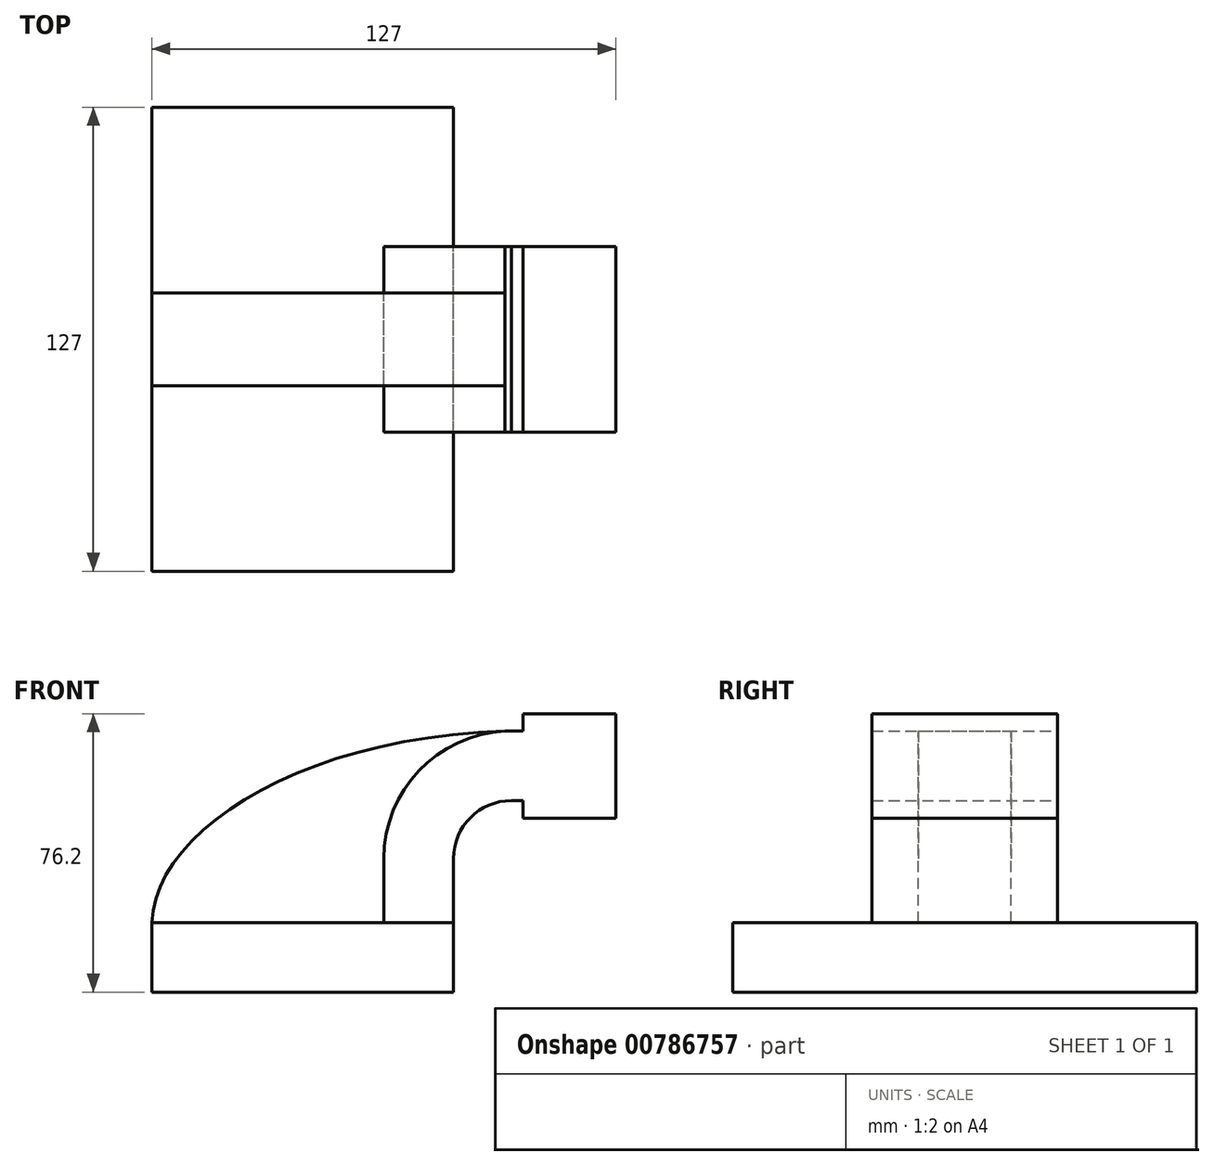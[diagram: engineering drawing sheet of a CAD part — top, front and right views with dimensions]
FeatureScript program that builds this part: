
annotation { "Feature Type Name" : "Feature", "Feature Type Description" : "" }
export const myFeature = defineFeature(function(context is Context, id is Id, definition is map)
    precondition{}
    {
        {
            var Q0;
            Q0=qCreatedBy(makeId("Front.planeOp"),FACE);
            var sketch = newSketch(context, id + "F0", { "sketchPlane" : qUnion([Q0])});
            skLineSegment(sketch, "E0.bottom", {"start": v(-41.28, 9.52) * mm, "end": v(41.27, 9.53) * mm});
            skLineSegment(sketch, "E0.top", {"start": v(-41.28, -9.53) * mm, "end": v(41.28, -9.53) * mm});
            skLineSegment(sketch, "E0.left", {"start": v(-41.28, 9.52) * mm, "end": v(-41.27, -9.53) * mm});
            skLineSegment(sketch, "E0.right", {"start": v(41.28, 9.53) * mm, "end": v(41.28, -9.52) * mm});
            skPoint(sketch, "E0.middle", {"position": v(0, 0) * mm});
            skLineSegment(sketch, "E1.bottom", {"start": v(60.32, 66.68) * mm, "end": v(111.12, 66.68) * mm});
            skLineSegment(sketch, "E1.top", {"start": v(60.32, 38.1) * mm, "end": v(111.12, 38.1) * mm});
            skLineSegment(sketch, "E1.left", {"start": v(60.32, 66.68) * mm, "end": v(60.32, 38.1) * mm});
            skLineSegment(sketch, "E1.right", {"start": v(111.12, 66.68) * mm, "end": v(111.12, 38.1) * mm});
            skPoint(sketch, "E1.middle", {"position": v(85.72, 52.39) * mm});
            skLineSegment(sketch, "E2", {"start": v(41.27, 9.53) * mm, "end": v(41.27, 27) * mm});
            skArc(sketch, "E3", {"start": v(41.27, 27) * mm, "mid": v(45.92, 38.23) * mm, "end": v(57.15, 42.88) * mm});
            skLineSegment(sketch, "E4", {"start": v(57.15, 42.88) * mm, "end": v(85.72, 42.88) * mm});
            skLineSegment(sketch, "E5.0", {"start": v(57.15, 61.93) * mm, "end": v(85.72, 61.93) * mm});
            skArc(sketch, "E5.1", {"start": v(22.22, 27) * mm, "mid": v(32.45, 51.7) * mm, "end": v(57.15, 61.93) * mm});
            skLineSegment(sketch, "E5.2", {"start": v(22.22, 9.53) * mm, "end": v(22.22, 27) * mm});
            skLineSegment(sketch, "E6", {"start": v(85.72, 38.1) * mm, "end": v(85.72, 66.68) * mm});
            skFitSpline(sketch, "E7", {"points": [v(-41.28, 9.52) * mm, v(57.15, 61.93) * mm], "startDerivative": vector(2.7, 75.83) * mm, "endDerivative": vector(171.45, 3.57) * mm});
            skSolve(sketch);
        }
        {
            var Q0;
            Q0=makeQuery(id+"F0.imprint","IMPRINT",FACE,{"disambiguationData":[TD([[makeQuery(id+"F0.imprint","IMPRINT",EDGE,{"derivedFrom":sQuery(id+"F0.wireOp",EDGE,"E0.top")}),1.0]])]});
            extrude(context, id + "F1", {"entities" : qUnion([Q0]), "endBound" : BoundingType.SYMMETRIC, "depth" : 127 * mm, "offsetDistance" : 25.4 * mm});
        }
        {
            var Q0;
            {var subQ1=sQuery(id+"F0.wireOp",EDGE,"E2");Q0=makeQuery(id+"F0.imprint","IMPRINT",FACE,{"disambiguationData":[TD([[makeQuery(id+"F0.imprint","IMPRINT",EDGE,{"derivedFrom":subQ1}),1.0]])]});}
            var Q1;
            {var subQ0=sQuery(id+"F0.wireOp",EDGE,"E1.left");var subQ1=sQuery(id+"F0.wireOp",EDGE,"E1.bottom");var subQ2=makeQuery(id+"F0.imprint","INTERSECT",VERTEX,{"derivedFrom":[subQ1,subQ0]});Q1=makeQuery(id+"F0.imprint","IMPRINT",FACE,{"disambiguationData":[TD([[makeQuery(id+"F0.imprint","IMPRINT",EDGE,{"disambiguationData":[TD([[subQ2,-1.0]])],"derivedFrom":subQ1}),-1.0]])]});}
            var Q2;
            {var subQ0=sQuery(id+"F0.wireOp",EDGE,"E1.left");var subQ1=sQuery(id+"F0.wireOp",EDGE,"E1.top");var subQ2=makeQuery(id+"F0.imprint","INTERSECT",VERTEX,{"derivedFrom":[subQ1,subQ0]});Q2=makeQuery(id+"F0.imprint","IMPRINT",FACE,{"disambiguationData":[TD([[makeQuery(id+"F0.imprint","IMPRINT",EDGE,{"disambiguationData":[TD([[subQ2,-1.0]])],"derivedFrom":subQ1}),1.0]])]});}
            var Q3;
            {var subQ0=sQuery(id+"F0.wireOp",EDGE,"E5.0");var subQ1=sQuery(id+"F0.wireOp",EDGE,"E1.left");var subQ2=makeQuery(id+"F0.imprint","INTERSECT",VERTEX,{"derivedFrom":[subQ1,subQ0]});Q3=makeQuery(id+"F0.imprint","IMPRINT",FACE,{"disambiguationData":[TD([[makeQuery(id+"F0.imprint","IMPRINT",EDGE,{"disambiguationData":[TD([[subQ2,-1.0]])],"derivedFrom":subQ1}),1.0]])]});}
            extrude(context, id + "F2", {"entities" : qUnion([Q0, Q1, Q2, Q3]), "endBound" : BoundingType.SYMMETRIC, "depth" : 50.8 * mm, "offsetDistance" : 25.4 * mm});
        }
        {
            var Q0;
            {var subQ3=sQuery(id+"F0.wireOp",EDGE,"E5.2");Q0=makeQuery(id+"F0.imprint","IMPRINT",FACE,{"disambiguationData":[TD([[makeQuery(id+"F0.imprint","IMPRINT",EDGE,{"derivedFrom":subQ3}),1.0]])]});}
            extrude(context, id + "F3", {"entities" : qUnion([Q0]), "endBound" : BoundingType.SYMMETRIC, "depth" : 25.4 * mm, "offsetDistance" : 25.4 * mm});
        }
    });
